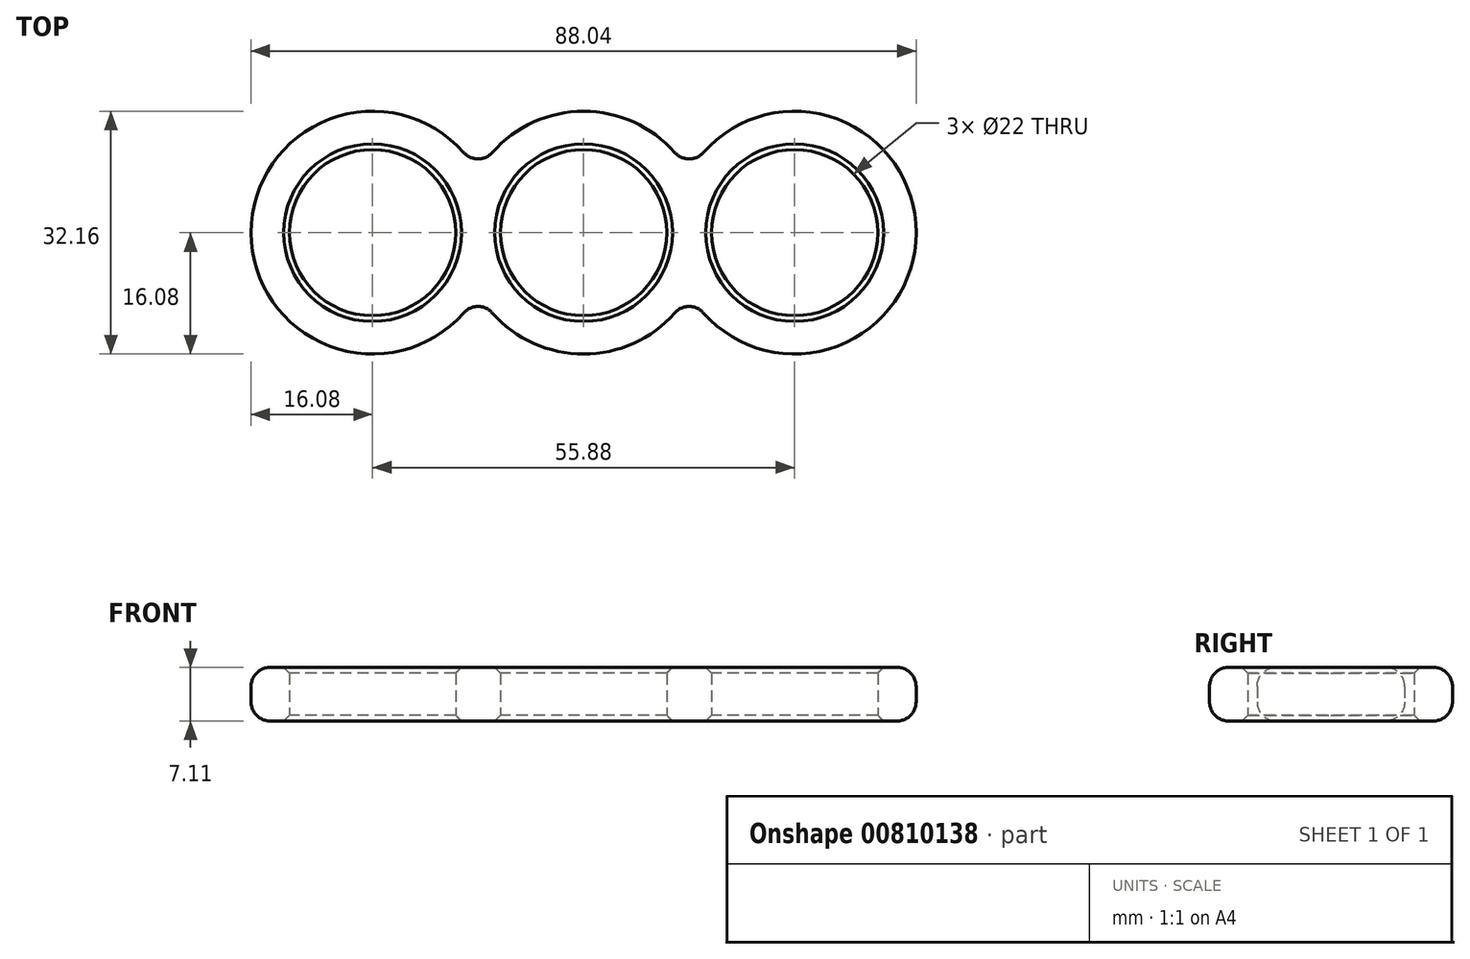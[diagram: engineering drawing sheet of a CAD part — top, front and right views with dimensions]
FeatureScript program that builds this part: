
annotation { "Feature Type Name" : "Feature", "Feature Type Description" : "" }
export const myFeature = defineFeature(function(context is Context, id is Id, definition is map)
    precondition{}
    {
        {
            var Q0;
            Q0=qCreatedBy(makeId("Top.planeOp"),FACE);
            var sketch = newSketch(context, id + "F0", { "sketchPlane" : qUnion([Q0])});
            skCircle(sketch, "E0", {"center": v(0, 0) * mm, "radius": 11 * mm});
            skCircle(sketch, "E1", {"center": v(27.94, 0) * mm, "radius": 11 * mm});
            skCircle(sketch, "E2.MirrorC", {"center": v(-27.94, 0) * mm, "radius": 11 * mm});
            skArc(sketch, "E3.0", {"start": v(-12.06, -10.63) * mm, "mid": v(0, -16.08) * mm, "end": v(12.06, -10.63) * mm});
            skArc(sketch, "E4.0", {"start": v(15.88, -10.63) * mm, "mid": v(44.02, 0) * mm, "end": v(15.88, 10.63) * mm});
            skArc(sketch, "E5.0", {"start": v(-15.88, -10.63) * mm, "mid": v(-44.02, 0) * mm, "end": v(-15.88, 10.63) * mm});
            skArc(sketch, "E6.trimOffspring", {"start": v(12.06, 10.63) * mm, "mid": v(0, 16.08) * mm, "end": v(-12.06, 10.63) * mm});
            skPoint(sketch, "E7.visualSharp", {"position": v(-13.97, 7.96) * mm});
            skArc(sketch, "E7.filletArc", {"start": v(-15.88, 10.63) * mm, "mid": v(-13.97, 9.77) * mm, "end": v(-12.06, 10.63) * mm});
            skPoint(sketch, "E8.visualSharp", {"position": v(13.97, 7.96) * mm});
            skArc(sketch, "E8.filletArc", {"start": v(12.06, 10.63) * mm, "mid": v(13.97, 9.77) * mm, "end": v(15.88, 10.63) * mm});
            skPoint(sketch, "E9.visualSharp", {"position": v(13.97, -7.96) * mm});
            skArc(sketch, "E9.filletArc", {"start": v(15.88, -10.63) * mm, "mid": v(13.97, -9.77) * mm, "end": v(12.06, -10.63) * mm});
            skPoint(sketch, "E10.visualSharp", {"position": v(-13.97, -7.96) * mm});
            skArc(sketch, "E10.filletArc", {"start": v(-12.06, -10.63) * mm, "mid": v(-13.97, -9.77) * mm, "end": v(-15.88, -10.63) * mm});
            skSolve(sketch);
        }
        {
            var Q0;
            Q0=makeQuery(id+"F0.imprint","IMPRINT",FACE,{"disambiguationData":[TD([[makeQuery(id+"F0.imprint","IMPRINT",EDGE,{"derivedFrom":sQuery(id+"F0.wireOp",EDGE,"E0")}),-1.0]])]});
            extrude(context, id + "F1", {"entities" : qUnion([Q0]), "depth" : 7.11 * mm, "offsetDistance" : 25.4 * mm});
        }
        {
            var Q0;
            Q0=makeQuery(id+"F1.opExtrude","CAP_EDGE",EDGE,{"disambiguationData":[OSD([sQuery(id+"F0.wireOp",EDGE,"E4.0")])],"isStart":true});
            var Q1;
            Q1=makeQuery(id+"F1.opExtrude","CAP_EDGE",EDGE,{"disambiguationData":[OSD([sQuery(id+"F0.wireOp",EDGE,"E5.0")])],"isStart":false});
            fillet(context, id + "F2", {"entities" : qUnion([Q0, Q1]), "radius" : 2.54 * mm, "tangentPropagation" : true, "allowEdgeOverflow" : false});
        }
        {
            var Q0;
            Q0=makeQuery(id+"F1.opExtrude","SWEPT_FACE",FACE,{"disambiguationData":[OSD([sQuery(id+"F0.wireOp",EDGE,"E2.MirrorC")])]});
            var Q1;
            Q1=makeQuery(id+"F1.opExtrude","SWEPT_FACE",FACE,{"disambiguationData":[OSD([sQuery(id+"F0.wireOp",EDGE,"E0")])]});
            var Q2;
            Q2=makeQuery(id+"F1.opExtrude","SWEPT_FACE",FACE,{"disambiguationData":[OSD([sQuery(id+"F0.wireOp",EDGE,"E1")])]});
            chamfer(context, id + "F3", {"entities" : qUnion([Q0, Q1, Q2]), "width" : 0.76 * mm, "tangentPropagation" : true});
        }
    });
